# Revit family: iFan_Eng
name_source: partatom
category: Mechanical Equipment
units: mm (PartAtom-declared; Revit-internal decimal feet)

## family parameters
Always vertical = Yes
Classification = None
Cut with Voids When Loaded = No
Part Type = Normal
Room Calculation Point = No
Round Connector Dimension = Use Diameter
Shared = No
Work Plane-Based = No

## types (2) — shared parameters
00_20_Manufacturer = Vents
00_20_Name = Axial fan
Amperage = 0 A
B = 152 mm  [stored 0.498688 ft]
Casing Material = Plastic, opaque, white
Description = For round channels
Frequency = 50 Hz
H = 206 mm  [stored 0.675853 ft]
Height = 206 mm  [stored 0.675853 ft]
L = 57 mm  [stored 0.187008 ft]
L1 = 29 mm  [stored 0.0951444 ft]
L2 = 28 mm  [stored 0.0918635 ft]
Length = 57 mm  [stored 0.187008 ft]
Load Classification = HVAC
Maintenance zone material = <By Category>
Manufacturer = Vents
Number of Fase = 1
Power = 4 W
URL = https://ventilation-system.com
Voltage = 230 V
Weight = 0.40 kg
Width = 152 mm  [stored 0.498688 ft]
zero-valued in all types: Default Elevation

## per-type parameters (varying)
| type | D | Diameter | Dy | Maximum Air Flow | Sound pressure level at 3 m distance |
| iFan 100 | 100 mm  [stored 0.328084 ft] | 100 mm  [stored 0.328084 ft] | 95 mm | 106.0 m³/h | 31 dBA |
| iFan 125 | 125 mm  [stored 0.410105 ft] | 125 mm  [stored 0.410105 ft] | 120 mm  [stored 0.393701 ft] | 133.0 m³/h | 32 dBA |

note: column(s) folded — value = type name in every type: 00_20_Type

note: [stored X ft] marks values corroborated as IEEE doubles in the binary element streams (Revit-internal decimal feet)
